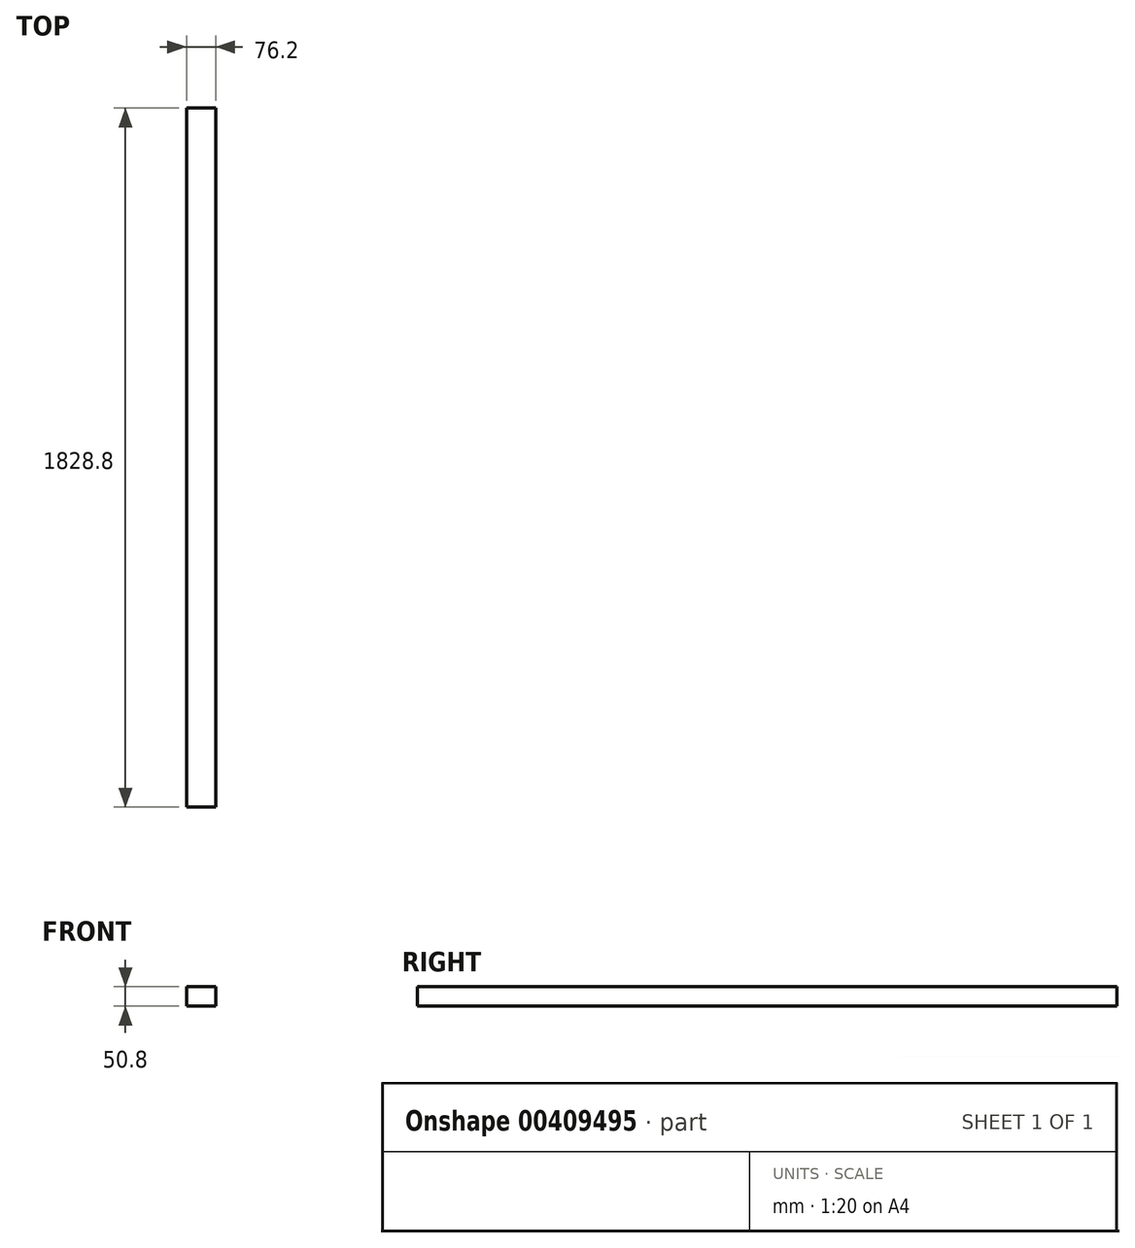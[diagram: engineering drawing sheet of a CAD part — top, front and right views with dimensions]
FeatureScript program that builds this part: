
annotation { "Feature Type Name" : "Feature", "Feature Type Description" : "" }
export const myFeature = defineFeature(function(context is Context, id is Id, definition is map)
    precondition{}
    {
        {
            var Q0;
            Q0=qCreatedBy(makeId("Front.planeOp"),FACE);
            var sketch = newSketch(context, id + "F0", { "sketchPlane" : qUnion([Q0])});
            skLineSegment(sketch, "E0.bottom", {"start": v(0, 0) * mm, "end": v(76.2, 0) * mm});
            skLineSegment(sketch, "E0.top", {"start": v(0, 50.8) * mm, "end": v(76.2, 50.8) * mm});
            skLineSegment(sketch, "E0.left", {"start": v(0, 0) * mm, "end": v(0, 50.8) * mm});
            skLineSegment(sketch, "E0.right", {"start": v(76.2, 0) * mm, "end": v(76.2, 50.8) * mm});
            skSolve(sketch);
        }
        {
            var Q0;
            Q0 = qSketchRegion(id + "F0", true);
            extrude(context, id + "F1", {"entities" : qUnion([Q0]), "depth" : 1828.8 * mm});
        }
    });
